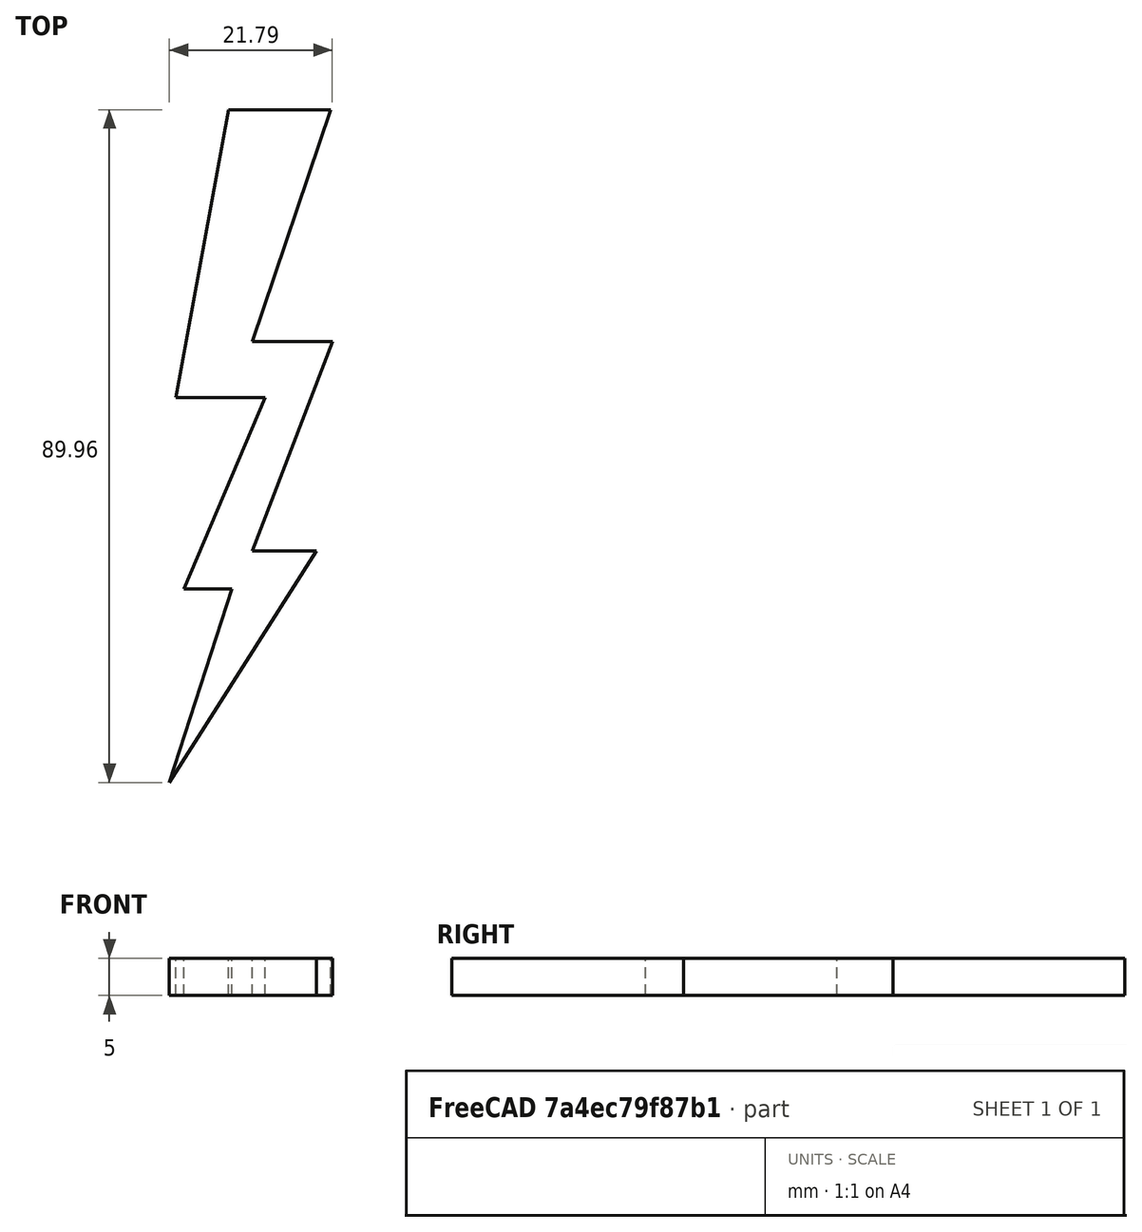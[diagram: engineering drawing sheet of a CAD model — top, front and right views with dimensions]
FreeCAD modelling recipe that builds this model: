
FCSTD DOCUMENT  (FreeCAD 1.0R39319 (Git))
Label: ojt1_t16r03_ray
License: All rights reserved
LicenseURL: https://en.wikipedia.org/wiki/All_rights_reserved
objects: Sketcher::SketchObject×1, PartDesign::Pad×1, PartDesign::Body×1
note: 6 computed .brp shape members not serialized (recipe doc carries the construction recipe); baked Part::Feature solids carry a one-line shape summary decoded from their .brp

FEATURE [Sketcher::SketchObject] Sketch
  ArcFitTolerance = 1e-06
  AttachmentSupport = -> [XY_Plane]
  FullyConstrained = false
  MakeInternals = false
  MapMode = 5
  sketch-geometry (11):
    g0: LineSegment StartX=19.765 StartY=42.3077 StartZ=0 EndX=33.4402 EndY=42.3077 EndZ=0
    g1: LineSegment StartX=33.4402 StartY=42.3077 StartZ=0 EndX=22.9701 EndY=11.3248 EndZ=0
    g2: LineSegment StartX=22.9701 StartY=11.3248 StartZ=0 EndX=33.6538 EndY=11.3248 EndZ=0
    g3: LineSegment StartX=33.6538 StartY=11.3248 StartZ=0 EndX=22.9701 EndY=-16.6667 EndZ=0
    g4: LineSegment StartX=22.9701 StartY=-16.6667 StartZ=0 EndX=31.5171 EndY=-16.6667 EndZ=0
    g5: LineSegment StartX=31.5171 StartY=-16.6667 StartZ=0 EndX=11.859 EndY=-47.6496 EndZ=0
    g6: LineSegment StartX=11.859 StartY=-47.6496 StartZ=0 EndX=20.1923 EndY=-21.7949 EndZ=0
    g7: LineSegment StartX=20.1923 StartY=-21.7949 StartZ=0 EndX=13.782 EndY=-21.7949 EndZ=0
    g8: LineSegment StartX=13.782 StartY=-21.7949 StartZ=0 EndX=24.6795 EndY=3.84616 EndZ=0
    g9: LineSegment StartX=24.6795 StartY=3.84616 StartZ=0 EndX=12.7137 EndY=3.84616 EndZ=0
    g10: LineSegment StartX=12.7137 StartY=3.84616 StartZ=0 EndX=19.765 EndY=42.3077 EndZ=0
  constraints (16):
    c: Horizontal(g0)
    c: Coincident(g0,g1)
    c: Coincident(g1,g2)
    c: Horizontal(g2)
    c: Coincident(g2,g3)
    c: Coincident(g3,g4)
    c: Horizontal(g4)
    c: Coincident(g4,g5)
    c: Coincident(g5,g6)
    c: Coincident(g6,g7)
    c: Horizontal(g7)
    c: Coincident(g7,g8)
    c: Coincident(g8,g9)
    c: Horizontal(g9)
    c: Coincident(g9,g10)
    c: Coincident(g10,g0)
FEATURE [PartDesign::Pad] Pad
  Direction = (0,0,1)
  Length = 5
  Length2 = 10
  Profile = -> Sketch
  ReferenceAxis = -> Sketch [N_Axis]
  Refine = true
  Suppressed = false
  Type = 0
FEATURE [PartDesign::Body] Body  label="Cos"
  AllowCompound = false
  Group = -> [Sketch,Pad]
  Origin = -> Origin
  Tip = -> Pad
